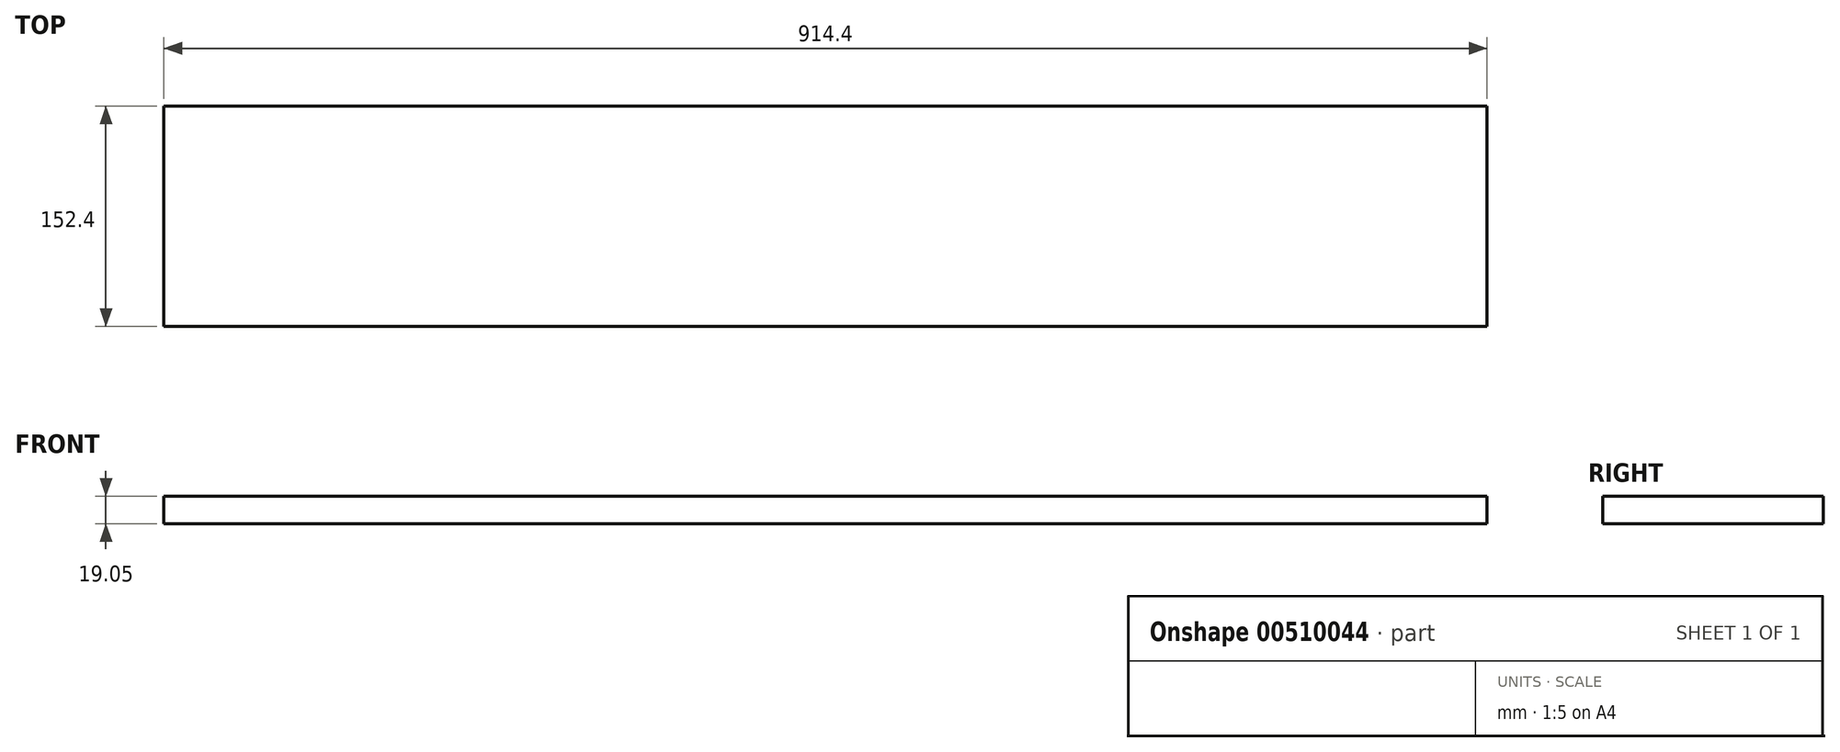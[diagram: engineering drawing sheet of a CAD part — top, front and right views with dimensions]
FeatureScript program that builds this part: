
annotation { "Feature Type Name" : "Feature", "Feature Type Description" : "" }
export const myFeature = defineFeature(function(context is Context, id is Id, definition is map)
    precondition{}
    {
        {
            var Q0;
            Q0=qCreatedBy(makeId("Top.planeOp"),FACE);
            var sketch = newSketch(context, id + "F0", { "sketchPlane" : qUnion([Q0])});
            skLineSegment(sketch, "E0.bottom", {"start": v(-449.78, 111.49) * mm, "end": v(464.62, 111.49) * mm});
            skLineSegment(sketch, "E0.top", {"start": v(-449.78, -40.91) * mm, "end": v(464.62, -40.91) * mm});
            skLineSegment(sketch, "E0.left", {"start": v(-449.78, 111.49) * mm, "end": v(-449.78, -40.91) * mm});
            skLineSegment(sketch, "E0.right", {"start": v(464.62, 111.49) * mm, "end": v(464.62, -40.91) * mm});
            skSolve(sketch);
        }
        {
            var Q0;
            Q0=makeQuery(id+"F0.imprint","IMPRINT",FACE,{"disambiguationData":[TD([[makeQuery(id+"F0.imprint","IMPRINT",EDGE,{"derivedFrom":sQuery(id+"F0.wireOp",EDGE,"E0.bottom")}),-1.0]])]});
            extrude(context, id + "F1", {"entities" : qUnion([Q0]), "depth" : 19.05 * mm, "offsetDistance" : 25.4 * mm});
        }
    });
